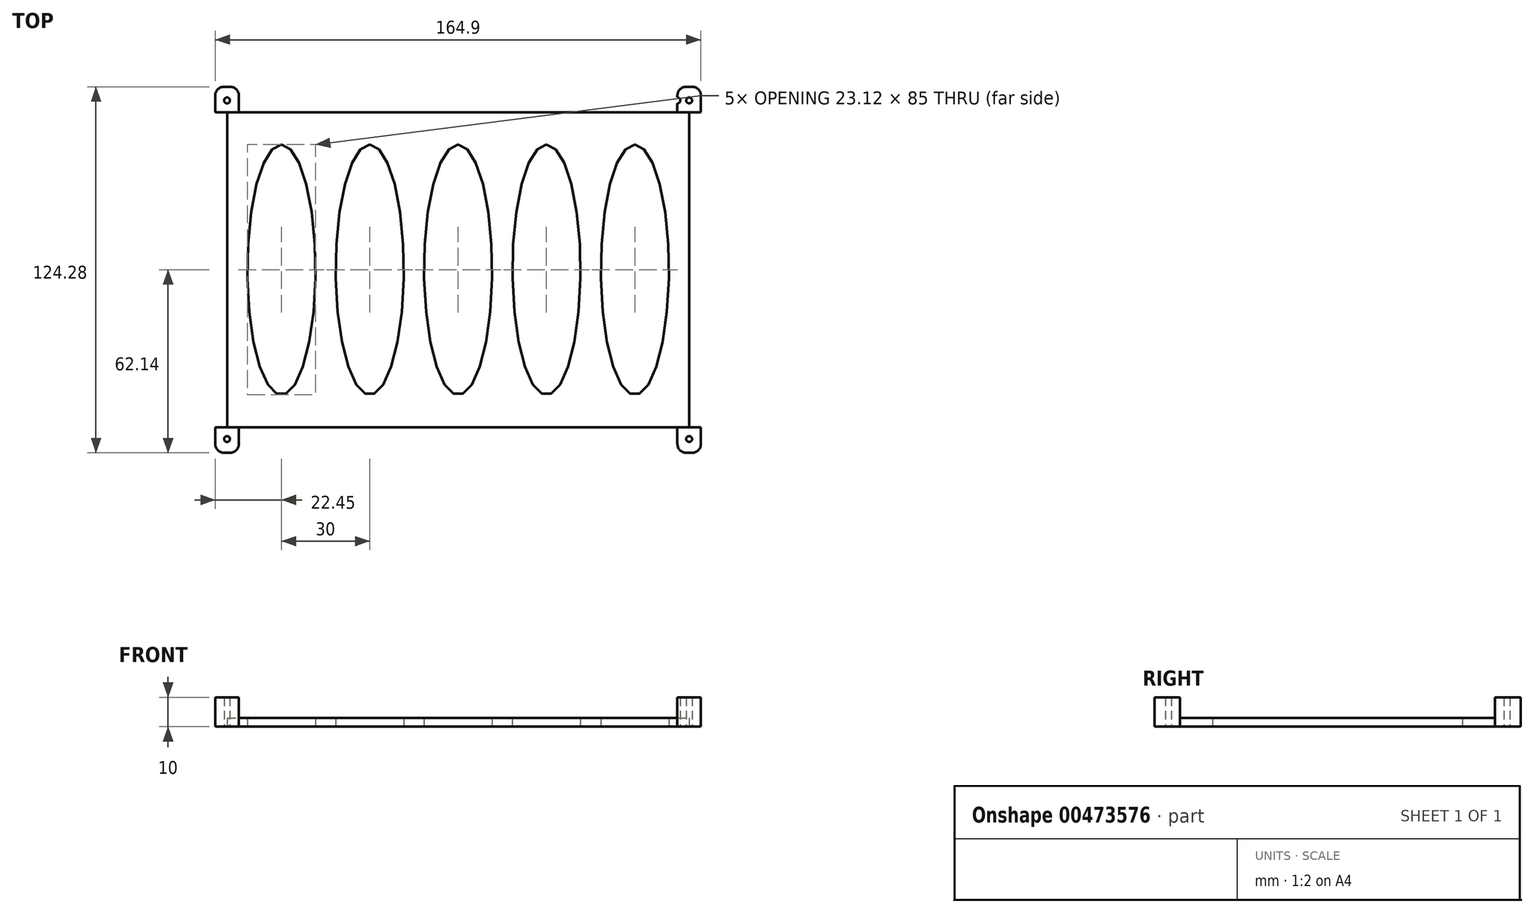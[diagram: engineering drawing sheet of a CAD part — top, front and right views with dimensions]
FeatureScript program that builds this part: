
annotation { "Feature Type Name" : "Feature", "Feature Type Description" : "" }
export const myFeature = defineFeature(function(context is Context, id is Id, definition is map)
    precondition{}
    {
        {
            var Q0;
            Q0=qCreatedBy(makeId("Top.planeOp"),FACE);
            var sketch = newSketch(context, id + "F0", { "sketchPlane" : qUnion([Q0])});
            skLineSegment(sketch, "E0.bottom", {"start": v(79.45, 62.14) * mm, "end": v(77.45, 62.14) * mm});
            skLineSegment(sketch, "E0.top", {"start": v(79.45, -62.14) * mm, "end": v(77.45, -62.14) * mm});
            skLineSegment(sketch, "E0.left", {"start": v(82.45, 59.14) * mm, "end": v(82.45, -59.14) * mm});
            skLineSegment(sketch, "E0.right", {"start": v(-82.45, 59.14) * mm, "end": v(-82.45, -59.14) * mm});
            skPoint(sketch, "E0.middle", {"position": v(0, 0) * mm});
            skLineSegment(sketch, "E1.bottom", {"start": v(82.45, 53.48) * mm, "end": v(-82.45, 53.48) * mm});
            skLineSegment(sketch, "E1.top", {"start": v(82.45, -53.48) * mm, "end": v(-82.45, -53.48) * mm});
            skLineSegment(sketch, "E1.left", {"start": v(82.45, 53.48) * mm, "end": v(82.45, -53.48) * mm});
            skLineSegment(sketch, "E1.right", {"start": v(-82.45, 53.48) * mm, "end": v(-82.45, -53.48) * mm});
            skLineSegment(sketch, "E2.left", {"start": v(74.45, 59.14) * mm, "end": v(74.45, -59.14) * mm});
            skLineSegment(sketch, "E2.right", {"start": v(-74.45, 59.13) * mm, "end": v(-74.45, -59.14) * mm});
            skLineSegment(sketch, "E3.bottom", {"start": v(78.45, 57.48) * mm, "end": v(74.45, 57.48) * mm});
            skLineSegment(sketch, "E3.top", {"start": v(78.45, -57.48) * mm, "end": v(-78.45, -57.48) * mm});
            skLineSegment(sketch, "E3.left", {"start": v(78.45, 57.48) * mm, "end": v(78.45, -57.48) * mm});
            skLineSegment(sketch, "E3.right", {"start": v(-78.45, 57.48) * mm, "end": v(-78.45, -57.48) * mm});
            skPoint(sketch, "E4", {"position": v(-78.45, 57.48) * mm});
            skPoint(sketch, "E5", {"position": v(78.45, 57.48) * mm});
            skPoint(sketch, "E6", {"position": v(78.45, -57.48) * mm});
            skPoint(sketch, "E7", {"position": v(-78.45, -57.48) * mm});
            skPoint(sketch, "E8.visualSharp", {"position": v(-82.45, 62.14) * mm});
            skArc(sketch, "E8.filletArc", {"start": v(-79.45, 62.14) * mm, "mid": v(-81.57, 61.26) * mm, "end": v(-82.45, 59.14) * mm});
            skPoint(sketch, "E9.visualSharp", {"position": v(-82.45, -62.14) * mm});
            skArc(sketch, "E9.filletArc", {"start": v(-82.45, -59.14) * mm, "mid": v(-81.57, -61.26) * mm, "end": v(-79.45, -62.14) * mm});
            skPoint(sketch, "E10.visualSharp", {"position": v(82.45, 62.14) * mm});
            skArc(sketch, "E10.filletArc", {"start": v(82.45, 59.14) * mm, "mid": v(81.57, 61.26) * mm, "end": v(79.45, 62.14) * mm});
            skPoint(sketch, "E11.visualSharp", {"position": v(82.45, -62.14) * mm});
            skArc(sketch, "E11.filletArc", {"start": v(79.45, -62.14) * mm, "mid": v(81.57, -61.26) * mm, "end": v(82.45, -59.14) * mm});
            skLineSegment(sketch, "E12.trimOffspring", {"start": v(-77.45, -62.14) * mm, "end": v(-79.45, -62.14) * mm});
            skLineSegment(sketch, "E13.trimOffspring", {"start": v(-77.45, 62.14) * mm, "end": v(-79.45, 62.14) * mm});
            skLineSegment(sketch, "E14.trimOffspring", {"start": v(-74.45, 57.48) * mm, "end": v(-78.45, 57.48) * mm});
            skPoint(sketch, "E15.visualSharp", {"position": v(74.45, 62.14) * mm});
            skArc(sketch, "E15.filletArc", {"start": v(77.45, 62.14) * mm, "mid": v(75.33, 61.26) * mm, "end": v(74.45, 59.14) * mm});
            skPoint(sketch, "E16.visualSharp", {"position": v(-74.45, -62.14) * mm});
            skArc(sketch, "E16.filletArc", {"start": v(-77.45, -62.14) * mm, "mid": v(-75.33, -61.26) * mm, "end": v(-74.45, -59.14) * mm});
            skPoint(sketch, "E17.visualSharp", {"position": v(74.45, -62.14) * mm});
            skArc(sketch, "E17.filletArc", {"start": v(74.45, -59.14) * mm, "mid": v(75.33, -61.26) * mm, "end": v(77.45, -62.14) * mm});
            skPoint(sketch, "E18.visualSharp", {"position": v(-74.45, 62.14) * mm});
            skArc(sketch, "E18.filletArc", {"start": v(-74.45, 59.13) * mm, "mid": v(-75.33, 61.26) * mm, "end": v(-77.45, 62.13) * mm});
            skSolve(sketch);
        }
        {
            var Q0;
            {var subQ0=sQuery(id+"F0.wireOp",EDGE,"E1.right");Q0=makeQuery(id+"F0.imprint","IMPRINT",FACE,{"disambiguationData":[TD([[makeQuery(id+"F0.imprint","IMPRINT",EDGE,{"derivedFrom":subQ0}),1.0]])]});}
            var Q1;
            {var subQ0=sQuery(id+"F0.wireOp",EDGE,"E2.right");var subQ1=sQuery(id+"F0.wireOp",EDGE,"E1.bottom");var subQ2=makeQuery(id+"F0.imprint","INTERSECT",VERTEX,{"derivedFrom":[subQ1,subQ0]});Q1=makeQuery(id+"F0.imprint","IMPRINT",FACE,{"disambiguationData":[TD([[makeQuery(id+"F0.imprint","IMPRINT",EDGE,{"disambiguationData":[TD([[subQ2,-1.0]])],"derivedFrom":subQ1}),-1.0]])]});}
            var Q2;
            {var subQ0=sQuery(id+"F0.wireOp",EDGE,"E2.left");var subQ1=sQuery(id+"F0.wireOp",EDGE,"E1.bottom");var subQ2=makeQuery(id+"F0.imprint","INTERSECT",VERTEX,{"derivedFrom":[subQ1,subQ0]});Q2=makeQuery(id+"F0.imprint","IMPRINT",FACE,{"disambiguationData":[TD([[makeQuery(id+"F0.imprint","IMPRINT",EDGE,{"disambiguationData":[TD([[subQ2,-1.0]])],"derivedFrom":subQ1}),1.0]])]});}
            var Q3;
            {var subQ0=sQuery(id+"F0.wireOp",EDGE,"E2.right");var subQ1=sQuery(id+"F0.wireOp",EDGE,"E1.bottom");var subQ2=makeQuery(id+"F0.imprint","INTERSECT",VERTEX,{"derivedFrom":[subQ1,subQ0]});Q3=makeQuery(id+"F0.imprint","IMPRINT",FACE,{"disambiguationData":[TD([[makeQuery(id+"F0.imprint","IMPRINT",EDGE,{"disambiguationData":[TD([[subQ2,-1.0]])],"derivedFrom":subQ1}),1.0]])]});}
            var Q4;
            {var subQ3=sQuery(id+"F0.wireOp",EDGE,"E3.bottom");var subQ8=sQuery(id+"F0.wireOp",EDGE,"E3.right");var subQ11=makeQuery(id+"F0.imprint","INTERSECT",VERTEX,{"derivedFrom":[subQ3,subQ8]});Q4=makeQuery(id+"F0.imprint","IMPRINT",FACE,{"disambiguationData":[TD([[makeQuery(id+"F0.imprint","IMPRINT",EDGE,{"disambiguationData":[TD([[subQ11,1.0]])],"derivedFrom":subQ3}),-1.0]])]});}
            var Q5;
            {var subQ3=sQuery(id+"F0.wireOp",EDGE,"E3.bottom");var subQ9=sQuery(id+"F0.wireOp",EDGE,"E3.left");var subQ11=makeQuery(id+"F0.imprint","INTERSECT",VERTEX,{"derivedFrom":[subQ3,subQ9]});Q5=makeQuery(id+"F0.imprint","IMPRINT",FACE,{"disambiguationData":[TD([[makeQuery(id+"F0.imprint","IMPRINT",EDGE,{"disambiguationData":[TD([[subQ11,-1.0]])],"derivedFrom":subQ3}),-1.0]])]});}
            var Q6;
            {var subQ0=sQuery(id+"F0.wireOp",EDGE,"E3.left");var subQ1=sQuery(id+"F0.wireOp",EDGE,"E1.bottom");var subQ2=makeQuery(id+"F0.imprint","INTERSECT",VERTEX,{"derivedFrom":[subQ1,subQ0]});Q6=makeQuery(id+"F0.imprint","IMPRINT",FACE,{"disambiguationData":[TD([[makeQuery(id+"F0.imprint","IMPRINT",EDGE,{"disambiguationData":[TD([[subQ2,-1.0]])],"derivedFrom":subQ1}),-1.0]])]});}
            var Q7;
            {var subQ0=sQuery(id+"F0.wireOp",EDGE,"E3.left");var subQ1=sQuery(id+"F0.wireOp",EDGE,"E1.bottom");var subQ2=makeQuery(id+"F0.imprint","INTERSECT",VERTEX,{"derivedFrom":[subQ1,subQ0]});Q7=makeQuery(id+"F0.imprint","IMPRINT",FACE,{"disambiguationData":[TD([[makeQuery(id+"F0.imprint","IMPRINT",EDGE,{"disambiguationData":[TD([[subQ2,-1.0]])],"derivedFrom":subQ1}),1.0]])]});}
            var Q8;
            {var subQ0=sQuery(id+"F0.wireOp",EDGE,"E1.left");Q8=makeQuery(id+"F0.imprint","IMPRINT",FACE,{"disambiguationData":[TD([[makeQuery(id+"F0.imprint","IMPRINT",EDGE,{"derivedFrom":subQ0}),-1.0]])]});}
            var Q9;
            {var subQ0=sQuery(id+"F0.wireOp",EDGE,"E3.left");var subQ1=sQuery(id+"F0.wireOp",EDGE,"E1.top");var subQ2=makeQuery(id+"F0.imprint","INTERSECT",VERTEX,{"derivedFrom":[subQ1,subQ0]});Q9=makeQuery(id+"F0.imprint","IMPRINT",FACE,{"disambiguationData":[TD([[makeQuery(id+"F0.imprint","IMPRINT",EDGE,{"disambiguationData":[TD([[subQ2,-1.0]])],"derivedFrom":subQ1}),1.0]])]});}
            var Q10;
            {var subQ3=sQuery(id+"F0.wireOp",EDGE,"E3.top");var subQ8=sQuery(id+"F0.wireOp",EDGE,"E3.left");var subQ11=makeQuery(id+"F0.imprint","INTERSECT",VERTEX,{"derivedFrom":[subQ3,subQ8]});Q10=makeQuery(id+"F0.imprint","IMPRINT",FACE,{"disambiguationData":[TD([[makeQuery(id+"F0.imprint","IMPRINT",EDGE,{"disambiguationData":[TD([[subQ11,-1.0]])],"derivedFrom":subQ3}),1.0]])]});}
            var Q11;
            {var subQ3=sQuery(id+"F0.wireOp",EDGE,"E3.top");var subQ8=sQuery(id+"F0.wireOp",EDGE,"E3.right");var subQ11=makeQuery(id+"F0.imprint","INTERSECT",VERTEX,{"derivedFrom":[subQ3,subQ8]});Q11=makeQuery(id+"F0.imprint","IMPRINT",FACE,{"disambiguationData":[TD([[makeQuery(id+"F0.imprint","IMPRINT",EDGE,{"disambiguationData":[TD([[subQ11,1.0]])],"derivedFrom":subQ3}),1.0]])]});}
            var Q12;
            {var subQ0=sQuery(id+"F0.wireOp",EDGE,"E2.right");var subQ1=sQuery(id+"F0.wireOp",EDGE,"E1.top");var subQ2=makeQuery(id+"F0.imprint","INTERSECT",VERTEX,{"derivedFrom":[subQ1,subQ0]});Q12=makeQuery(id+"F0.imprint","IMPRINT",FACE,{"disambiguationData":[TD([[makeQuery(id+"F0.imprint","IMPRINT",EDGE,{"disambiguationData":[TD([[subQ2,-1.0]])],"derivedFrom":subQ1}),1.0]])]});}
            var Q13;
            {var subQ8=sQuery(id+"F0.wireOp",EDGE,"E8.filletArc");Q13=makeQuery(id+"F0.imprint","IMPRINT",FACE,{"disambiguationData":[TD([[makeQuery(id+"F0.imprint","IMPRINT",EDGE,{"derivedFrom":subQ8}),1.0]])]});}
            extrude(context, id + "F1", {"entities" : qUnion([Q0, Q1, Q2, Q3, Q4, Q5, Q6, Q7, Q8, Q9, Q10, Q11, Q12, Q13]), "depth" : 3 * mm});
        }
        {
            var Q0;
            Q0=makeQuery(id+"F0.imprint","IMPRINT",FACE,{"disambiguationData":[TD([[makeQuery(id+"F0.imprint","IMPRINT",EDGE,{"derivedFrom":sQuery(id+"F0.wireOp",EDGE,"E0.bottom")}),1.0]])]});
            var Q1;
            {var subQ5=sQuery(id+"F0.wireOp",EDGE,"E3.bottom");Q1=makeQuery(id+"F0.imprint","IMPRINT",FACE,{"disambiguationData":[TD([[makeQuery(id+"F0.imprint","IMPRINT",EDGE,{"derivedFrom":subQ5}),1.0]])]});}
            var Q2;
            {var subQ8=sQuery(id+"F0.wireOp",EDGE,"E8.filletArc");Q2=makeQuery(id+"F0.imprint","IMPRINT",FACE,{"disambiguationData":[TD([[makeQuery(id+"F0.imprint","IMPRINT",EDGE,{"derivedFrom":subQ8}),1.0]])]});}
            var Q3;
            {var subQ5=sQuery(id+"F0.wireOp",EDGE,"E14.trimOffspring");Q3=makeQuery(id+"F0.imprint","IMPRINT",FACE,{"disambiguationData":[TD([[makeQuery(id+"F0.imprint","IMPRINT",EDGE,{"derivedFrom":subQ5}),1.0]])]});}
            var Q4;
            Q4=makeQuery(id+"F0.imprint","IMPRINT",FACE,{"disambiguationData":[TD([[makeQuery(id+"F0.imprint","IMPRINT",EDGE,{"derivedFrom":sQuery(id+"F0.wireOp",EDGE,"E0.top")}),-1.0]])]});
            var Q5;
            {var subQ0=sQuery(id+"F0.wireOp",EDGE,"E3.left");var subQ1=sQuery(id+"F0.wireOp",EDGE,"E1.top");var subQ2=makeQuery(id+"F0.imprint","INTERSECT",VERTEX,{"derivedFrom":[subQ1,subQ0]});Q5=makeQuery(id+"F0.imprint","IMPRINT",FACE,{"disambiguationData":[TD([[makeQuery(id+"F0.imprint","IMPRINT",EDGE,{"disambiguationData":[TD([[subQ2,-1.0]])],"derivedFrom":subQ1}),1.0]])]});}
            var Q6;
            {var subQ6=sQuery(id+"F0.wireOp",EDGE,"E9.filletArc");Q6=makeQuery(id+"F0.imprint","IMPRINT",FACE,{"disambiguationData":[TD([[makeQuery(id+"F0.imprint","IMPRINT",EDGE,{"derivedFrom":subQ6}),1.0]])]});}
            var Q7;
            {var subQ0=sQuery(id+"F0.wireOp",EDGE,"E2.right");var subQ1=sQuery(id+"F0.wireOp",EDGE,"E1.top");var subQ2=makeQuery(id+"F0.imprint","INTERSECT",VERTEX,{"derivedFrom":[subQ1,subQ0]});Q7=makeQuery(id+"F0.imprint","IMPRINT",FACE,{"disambiguationData":[TD([[makeQuery(id+"F0.imprint","IMPRINT",EDGE,{"disambiguationData":[TD([[subQ2,-1.0]])],"derivedFrom":subQ1}),1.0]])]});}
            extrude(context, id + "F2", {"entities" : qUnion([Q0, Q1, Q2, Q3, Q4, Q5, Q6, Q7]), "operationType" : NewBodyOperationType.ADD, "depth" : 10 * mm});
        }
        {
            var Q0;
            Q0=sQuery(id+"F0.wireOp",VERTEX,"E3.bottom.end");
            var Q1;
            Q1=sQuery(id+"F0.wireOp",VERTEX,"E3.left.start");
            var Q2;
            Q2=sQuery(id+"F0.wireOp",VERTEX,"E6");
            var Q3;
            Q3=sQuery(id+"F0.wireOp",VERTEX,"E3.top.end");
            var Q4;
            Q4=sQuery(id+"F0.wireOp",VERTEX,"E4");
            var Q5;
            Q5=makeQuery(id+"F1.opExtrude","SWEPT_BODY",BODY,{"disambiguationData":[OSD([sQuery(id+"F0.wireOp",EDGE,"E0.bottom"),sQuery(id+"F0.wireOp",EDGE,"E0.top"),sQuery(id+"F0.wireOp",EDGE,"E0.left"),sQuery(id+"F0.wireOp",EDGE,"E0.right"),sQuery(id+"F0.wireOp",EDGE,"E1.bottom"),sQuery(id+"F0.wireOp",EDGE,"E1.top"),sQuery(id+"F0.wireOp",EDGE,"E1.left"),sQuery(id+"F0.wireOp",EDGE,"E1.right"),sQuery(id+"F0.wireOp",EDGE,"E2.left"),sQuery(id+"F0.wireOp",EDGE,"E2.right")])]});
            hole(context, id + "F3", {"style" : HoleStyle.SIMPLE, "endStyle" : HoleEndStyle.THROUGH, "oppositeDirection" : true, "holeDiameter" : 2 * mm, "isTappedThrough" : true, "tappedDepth" : 12 * mm, "tapClearance" : 3, "locations" : qUnion([Q0, Q1, Q2, Q3, Q4]), "scope" : qUnion([Q5])});
        }
        {
            var Q0;
            Q0=makeQuery(id+"F1.opExtrude","CAP_FACE",FACE,{"disambiguationData":[OSD([sQuery(id+"F0.wireOp",EDGE,"E0.bottom"),sQuery(id+"F0.wireOp",EDGE,"E0.top"),sQuery(id+"F0.wireOp",EDGE,"E0.left"),sQuery(id+"F0.wireOp",EDGE,"E0.right"),sQuery(id+"F0.wireOp",EDGE,"E1.bottom"),sQuery(id+"F0.wireOp",EDGE,"E1.top"),sQuery(id+"F0.wireOp",EDGE,"E1.left"),sQuery(id+"F0.wireOp",EDGE,"E1.right"),sQuery(id+"F0.wireOp",EDGE,"E2.left"),sQuery(id+"F0.wireOp",EDGE,"E2.right"),sQuery(id+"F0.wireOp",EDGE,"E8.filletArc"),sQuery(id+"F0.wireOp",EDGE,"E9.filletArc"),sQuery(id+"F0.wireOp",EDGE,"E10.filletArc"),sQuery(id+"F0.wireOp",EDGE,"E11.filletArc"),sQuery(id+"F0.wireOp",EDGE,"E12.trimOffspring"),sQuery(id+"F0.wireOp",EDGE,"E13.trimOffspring"),sQuery(id+"F0.wireOp",EDGE,"E15.filletArc"),sQuery(id+"F0.wireOp",EDGE,"E16.filletArc"),sQuery(id+"F0.wireOp",EDGE,"E17.filletArc"),sQuery(id+"F0.wireOp",EDGE,"E18.filletArc")])],"isStart":false});
            var sketch = newSketch(context, id + "F4", { "sketchPlane" : qUnion([Q0])});
            skEllipse(sketch, "E19", {"center": v(0, 0) * mm, "majorRadius": 42.5 * mm, "minorRadius": 11.56 * mm, "majorAxis": v(0, 1)});
            skEllipse(sketch, "E20.1.0.0", {"center": v(30, 0) * mm, "majorRadius": 42.5 * mm, "minorRadius": 11.56 * mm, "majorAxis": v(0, 1)});
            skEllipse(sketch, "E20.2.0.0", {"center": v(60, 0) * mm, "majorRadius": 42.5 * mm, "minorRadius": 11.56 * mm, "majorAxis": v(0, 1)});
            skLineSegment(sketch, "E20.direction1", {"start": v(0, 0) * mm, "end": v(30, 0) * mm, "construction": true});
            skEllipse(sketch, "E21.1.0.0", {"center": v(-30, 0) * mm, "majorRadius": 42.5 * mm, "minorRadius": 11.56 * mm, "majorAxis": v(0, 1)});
            skEllipse(sketch, "E21.2.0.0", {"center": v(-60, 0) * mm, "majorRadius": 42.5 * mm, "minorRadius": 11.56 * mm, "majorAxis": v(0, 1)});
            skLineSegment(sketch, "E21.direction1", {"start": v(0, 0) * mm, "end": v(-30, 0) * mm, "construction": true});
            skSolve(sketch);
        }
        {
            var Q0;
            Q0=makeQuery(id+"F4.imprint","IMPRINT",FACE,{"disambiguationData":[TD([[makeQuery(id+"F4.imprint","IMPRINT",EDGE,{"derivedFrom":sQuery(id+"F4.wireOp",EDGE,"E21.2.0.0")}),1.0]])]});
            var Q1;
            Q1=makeQuery(id+"F4.imprint","IMPRINT",FACE,{"disambiguationData":[TD([[makeQuery(id+"F4.imprint","IMPRINT",EDGE,{"derivedFrom":sQuery(id+"F4.wireOp",EDGE,"E21.1.0.0")}),1.0]])]});
            var Q2;
            Q2=makeQuery(id+"F4.imprint","IMPRINT",FACE,{"disambiguationData":[TD([[makeQuery(id+"F4.imprint","IMPRINT",EDGE,{"derivedFrom":sQuery(id+"F4.wireOp",EDGE,"E19")}),1.0]])]});
            var Q3;
            Q3=makeQuery(id+"F4.imprint","IMPRINT",FACE,{"disambiguationData":[TD([[makeQuery(id+"F4.imprint","IMPRINT",EDGE,{"derivedFrom":sQuery(id+"F4.wireOp",EDGE,"E20.1.0.0")}),1.0]])]});
            var Q4;
            Q4=makeQuery(id+"F4.imprint","IMPRINT",FACE,{"disambiguationData":[TD([[makeQuery(id+"F4.imprint","IMPRINT",EDGE,{"derivedFrom":sQuery(id+"F4.wireOp",EDGE,"E20.2.0.0")}),1.0]])]});
            extrude(context, id + "F5", {"entities" : qUnion([Q0, Q1, Q2, Q3, Q4]), "operationType" : NewBodyOperationType.REMOVE, "oppositeDirection" : true, "depth" : 25 * mm});
        }
    });
